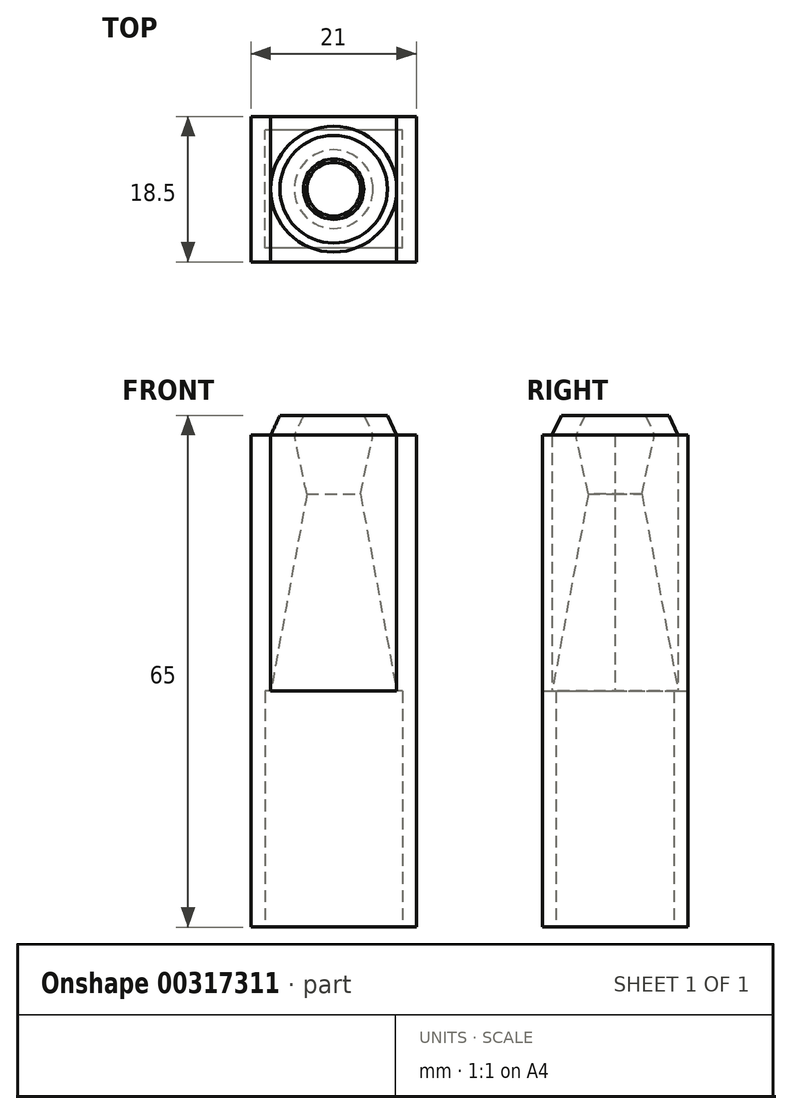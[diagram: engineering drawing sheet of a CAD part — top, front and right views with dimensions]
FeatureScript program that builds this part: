
annotation { "Feature Type Name" : "Feature", "Feature Type Description" : "" }
export const myFeature = defineFeature(function(context is Context, id is Id, definition is map)
    precondition{}
    {
        {
            var Q0;
            Q0=qCreatedBy(makeId("Front.planeOp"),FACE);
            var sketch = newSketch(context, id + "F0", { "sketchPlane" : qUnion([Q0])});
            skLineSegment(sketch, "E0", {"start": v(10, 4.68) * mm, "end": v(26, 4.68) * mm});
            skLineSegment(sketch, "E1", {"start": v(10, 4.68) * mm, "end": v(10, 67.18) * mm});
            skLineSegment(sketch, "E2", {"start": v(10, 67.18) * mm, "end": v(26, 67.18) * mm});
            skLineSegment(sketch, "E3", {"start": v(26, 67.18) * mm, "end": v(26, 4.68) * mm});
            skLineSegment(sketch, "E4", {"start": v(10, 4.68) * mm, "end": v(7.5, 4.68) * mm});
            skLineSegment(sketch, "E5", {"start": v(7.5, 4.68) * mm, "end": v(7.5, 67.18) * mm});
            skLineSegment(sketch, "E6", {"start": v(7.5, 67.18) * mm, "end": v(10, 67.18) * mm});
            skLineSegment(sketch, "E7", {"start": v(26, 67.18) * mm, "end": v(28.5, 67.18) * mm});
            skLineSegment(sketch, "E8", {"start": v(28.5, 67.18) * mm, "end": v(28.5, 4.68) * mm});
            skLineSegment(sketch, "E9", {"start": v(28.5, 4.68) * mm, "end": v(26, 4.68) * mm});
            skLineSegment(sketch, "E10", {"start": v(18, 4.68) * mm, "end": v(18, 69.68) * mm, "construction": true});
            skLineSegment(sketch, "E11", {"start": v(7.5, 67.18) * mm, "end": v(10, 69.68) * mm});
            skLineSegment(sketch, "E12", {"start": v(10, 69.68) * mm, "end": v(10, 67.18) * mm});
            skLineSegment(sketch, "E13", {"start": v(28.5, 67.18) * mm, "end": v(26, 69.68) * mm});
            skLineSegment(sketch, "E14", {"start": v(26, 69.68) * mm, "end": v(26, 67.18) * mm});
            skLineSegment(sketch, "E15", {"start": v(10, 69.68) * mm, "end": v(26, 69.68) * mm, "construction": true});
            skLineSegment(sketch, "E16", {"start": v(10, 67.18) * mm, "end": v(11.6, 59.68) * mm});
            skLineSegment(sketch, "E17", {"start": v(26, 67.18) * mm, "end": v(24.4, 59.68) * mm});
            skLineSegment(sketch, "E18", {"start": v(24.4, 59.68) * mm, "end": v(11.6, 59.68) * mm});
            skLineSegment(sketch, "E19", {"start": v(18, 4.68) * mm, "end": v(18, 59.68) * mm});
            skLineSegment(sketch, "E20", {"start": v(10, 34.68) * mm, "end": v(26, 34.68) * mm, "construction": true});
            skLineSegment(sketch, "E21", {"start": v(11.6, 59.68) * mm, "end": v(10, 34.68) * mm});
            skLineSegment(sketch, "E22", {"start": v(24.4, 59.68) * mm, "end": v(26, 34.68) * mm});
            skLineSegment(sketch, "E23", {"start": v(10, 34.68) * mm, "end": v(26, 34.68) * mm});
            skLineSegment(sketch, "E24", {"start": v(26, 67.18) * mm, "end": v(24.83, 69.68) * mm});
            skLineSegment(sketch, "E25", {"start": v(24.83, 69.68) * mm, "end": v(26, 69.68) * mm});
            skLineSegment(sketch, "E26", {"start": v(10, 67.18) * mm, "end": v(11.16, 69.68) * mm});
            skLineSegment(sketch, "E27", {"start": v(11.16, 69.68) * mm, "end": v(10, 69.68) * mm});
            skLineSegment(sketch, "E28", {"start": v(23, 67.18) * mm, "end": v(21.4, 59.68) * mm});
            skLineSegment(sketch, "E29", {"start": v(13, 67.18) * mm, "end": v(14.6, 59.68) * mm});
            skLineSegment(sketch, "E30", {"start": v(13, 67.18) * mm, "end": v(13, 69.68) * mm});
            skLineSegment(sketch, "E31", {"start": v(23, 67.18) * mm, "end": v(23, 69.68) * mm});
            skLineSegment(sketch, "E32", {"start": v(13, 67.18) * mm, "end": v(14.16, 69.68) * mm});
            skLineSegment(sketch, "E33", {"start": v(14.16, 69.68) * mm, "end": v(13, 69.68) * mm});
            skLineSegment(sketch, "E34", {"start": v(23, 67.18) * mm, "end": v(21.83, 69.68) * mm});
            skLineSegment(sketch, "E35", {"start": v(21.83, 69.68) * mm, "end": v(23, 69.68) * mm});
            skLineSegment(sketch, "E36", {"start": v(13, 69.68) * mm, "end": v(11.16, 69.68) * mm});
            skLineSegment(sketch, "E37", {"start": v(23, 69.68) * mm, "end": v(24.83, 69.68) * mm});
            skLineSegment(sketch, "E38", {"start": v(14.6, 59.68) * mm, "end": v(10, 34.68) * mm});
            skLineSegment(sketch, "E39", {"start": v(21.4, 59.68) * mm, "end": v(26, 34.68) * mm});
            skSolve(sketch);
        }
        {
            var Q0;
            {var subQ0=sQuery(id+"F0.wireOp",EDGE,"E22");Q0=makeQuery(id+"F0.imprint","IMPRINT",FACE,{"disambiguationData":[TD([[makeQuery(id+"F0.imprint","IMPRINT",EDGE,{"derivedFrom":subQ0}),-1.0]])]});}
            var Q1;
            {var subQ0=sQuery(id+"F0.wireOp",EDGE,"E17");Q1=makeQuery(id+"F0.imprint","IMPRINT",FACE,{"disambiguationData":[TD([[makeQuery(id+"F0.imprint","IMPRINT",EDGE,{"derivedFrom":subQ0}),-1.0]])]});}
            var Q2;
            {var subQ0=sQuery(id+"F0.wireOp",EDGE,"E24");Q2=makeQuery(id+"F0.imprint","IMPRINT",FACE,{"disambiguationData":[TD([[makeQuery(id+"F0.imprint","IMPRINT",EDGE,{"derivedFrom":subQ0}),1.0]])]});}
            var Q3;
            Q3=makeQuery(id+"F0.imprint","IMPRINT",FACE,{"disambiguationData":[TD([[makeQuery(id+"F0.imprint","IMPRINT",EDGE,{"derivedFrom":sQuery(id+"F0.wireOp",EDGE,"E31")}),1.0]])]});
            var Q4;
            {var subQ0=sQuery(id+"F0.wireOp",EDGE,"E17");Q4=makeQuery(id+"F0.imprint","IMPRINT",FACE,{"disambiguationData":[TD([[makeQuery(id+"F0.imprint","IMPRINT",EDGE,{"derivedFrom":subQ0}),1.0]])]});}
            var Q5;
            Q5=sQuery(id+"F0.wireOp",EDGE,"E10");
            revolve(context, id + "F1", {"entities" : qUnion([Q0, Q1, Q2, Q3, Q4]), "axis" : qUnion([Q5]), "revolveType" : RevolveType.FULL});
        }
        {
            var Q0;
            {var subQ3=sQuery(id+"F0.wireOp",EDGE,"E4");Q0=makeQuery(id+"F0.imprint","IMPRINT",FACE,{"disambiguationData":[TD([[makeQuery(id+"F0.imprint","IMPRINT",EDGE,{"derivedFrom":subQ3}),-1.0]])]});}
            var Q1;
            {var subQ3=sQuery(id+"F0.wireOp",EDGE,"E7");Q1=makeQuery(id+"F0.imprint","IMPRINT",FACE,{"disambiguationData":[TD([[makeQuery(id+"F0.imprint","IMPRINT",EDGE,{"derivedFrom":subQ3}),-1.0]])]});}
            var Q2;
            {var subQ1=sQuery(id+"F0.wireOp",EDGE,"E0");var subQ3=sQuery(id+"F0.wireOp",EDGE,"E19");var subQ4=makeQuery(id+"F0.imprint","INTERSECT",VERTEX,{"derivedFrom":[subQ1,subQ3]});Q2=makeQuery(id+"F0.imprint","IMPRINT",FACE,{"disambiguationData":[TD([[makeQuery(id+"F0.imprint","IMPRINT",EDGE,{"disambiguationData":[TD([[subQ4,-1.0]])],"derivedFrom":subQ3}),1.0]])]});}
            var Q3;
            {var subQ1=sQuery(id+"F0.wireOp",EDGE,"E0");var subQ3=sQuery(id+"F0.wireOp",EDGE,"E19");var subQ4=makeQuery(id+"F0.imprint","INTERSECT",VERTEX,{"derivedFrom":[subQ1,subQ3]});Q3=makeQuery(id+"F0.imprint","IMPRINT",FACE,{"disambiguationData":[TD([[makeQuery(id+"F0.imprint","IMPRINT",EDGE,{"disambiguationData":[TD([[subQ4,-1.0]])],"derivedFrom":subQ3}),-1.0]])]});}
            extrude(context, id + "F2", {"entities" : qUnion([Q0, Q1, Q2, Q3]), "endBound" : BoundingType.SYMMETRIC, "depth" : 18.5 * mm});
        }
        {
            var Q0;
            Q0=makeQuery(id+"F2.opExtrude","SWEPT_FACE",FACE,{"disambiguationData":[OSD([sQuery(id+"F0.wireOp",EDGE,"E23")])]});
            var sketch = newSketch(context, id + "F3", { "sketchPlane" : qUnion([Q0])});
            skCircle(sketch, "E40.0", {"center": v(18, 0) * mm, "radius": 8 * mm});
            skLineSegment(sketch, "E41.0.0", {"start": v(26, 9.25) * mm, "end": v(10, 9.25) * mm});
            skLineSegment(sketch, "E41.0.1", {"start": v(10, 9.25) * mm, "end": v(10, -9.25) * mm});
            skLineSegment(sketch, "E41.0.2", {"start": v(10, -9.25) * mm, "end": v(26, -9.25) * mm});
            skLineSegment(sketch, "E41.0.3", {"start": v(26, -9.25) * mm, "end": v(26, 9.25) * mm});
            skSolve(sketch);
        }
        {
            var Q0;
            {var subQ5=sQuery(id+"F3.wireOp",EDGE,"E41.0.2");Q0=makeQuery(id+"F3.imprint","IMPRINT",FACE,{"disambiguationData":[TD([[makeQuery(id+"F3.imprint","IMPRINT",EDGE,{"derivedFrom":subQ5}),1.0]])]});}
            var Q1;
            {var subQ5=sQuery(id+"F3.wireOp",EDGE,"E41.0.0");Q1=makeQuery(id+"F3.imprint","IMPRINT",FACE,{"disambiguationData":[TD([[makeQuery(id+"F3.imprint","IMPRINT",EDGE,{"derivedFrom":subQ5}),-1.0]])]});}
            var Q2;
            Q2=makeQuery(id+"F2.opExtrude","SWEPT_FACE",FACE,{"disambiguationData":[OSD([sQuery(id+"F0.wireOp",EDGE,"E6")])]});
            extrude(context, id + "F4", {"entities" : qUnion([Q0, Q1]), "endBound" : BoundingType.UP_TO_SURFACE, "endBoundEntityFace" : qUnion([Q2]), "depth" : 25 * mm});
        }
        {
            var Q0;
            Q0=makeQuery(id+"F2.opExtrude","SWEPT_FACE",FACE,{"disambiguationData":[OSD([sQuery(id+"F0.wireOp",EDGE,"E0"),sQuery(id+"F0.wireOp",EDGE,"E4"),sQuery(id+"F0.wireOp",EDGE,"E9")])]});
            var sketch = newSketch(context, id + "F5", { "sketchPlane" : qUnion([Q0])});
            skPoint(sketch, "E42.0", {"position": v(18, 9.25) * mm});
            skPoint(sketch, "E43.0", {"position": v(28.5, 0) * mm});
            skLineSegment(sketch, "E44.bottom", {"start": v(26.75, 7.5) * mm, "end": v(9.25, 7.5) * mm});
            skLineSegment(sketch, "E44.top", {"start": v(26.75, -7.5) * mm, "end": v(9.25, -7.5) * mm});
            skLineSegment(sketch, "E44.left", {"start": v(26.75, 7.5) * mm, "end": v(26.75, -7.5) * mm});
            skLineSegment(sketch, "E44.right", {"start": v(9.25, 7.5) * mm, "end": v(9.25, -7.5) * mm});
            skPoint(sketch, "E44.middle", {"position": v(18, 0) * mm});
            skSolve(sketch);
        }
        {
            var Q0;
            Q0=makeQuery(id+"F5.imprint","IMPRINT",FACE,{"disambiguationData":[TD([[makeQuery(id+"F5.imprint","IMPRINT",EDGE,{"derivedFrom":sQuery(id+"F5.wireOp",EDGE,"E44.bottom")}),1.0]])]});
            extrude(context, id + "F6", {"entities" : qUnion([Q0]), "operationType" : NewBodyOperationType.REMOVE, "oppositeDirection" : true, "depth" : 30 * mm});
        }
    });
